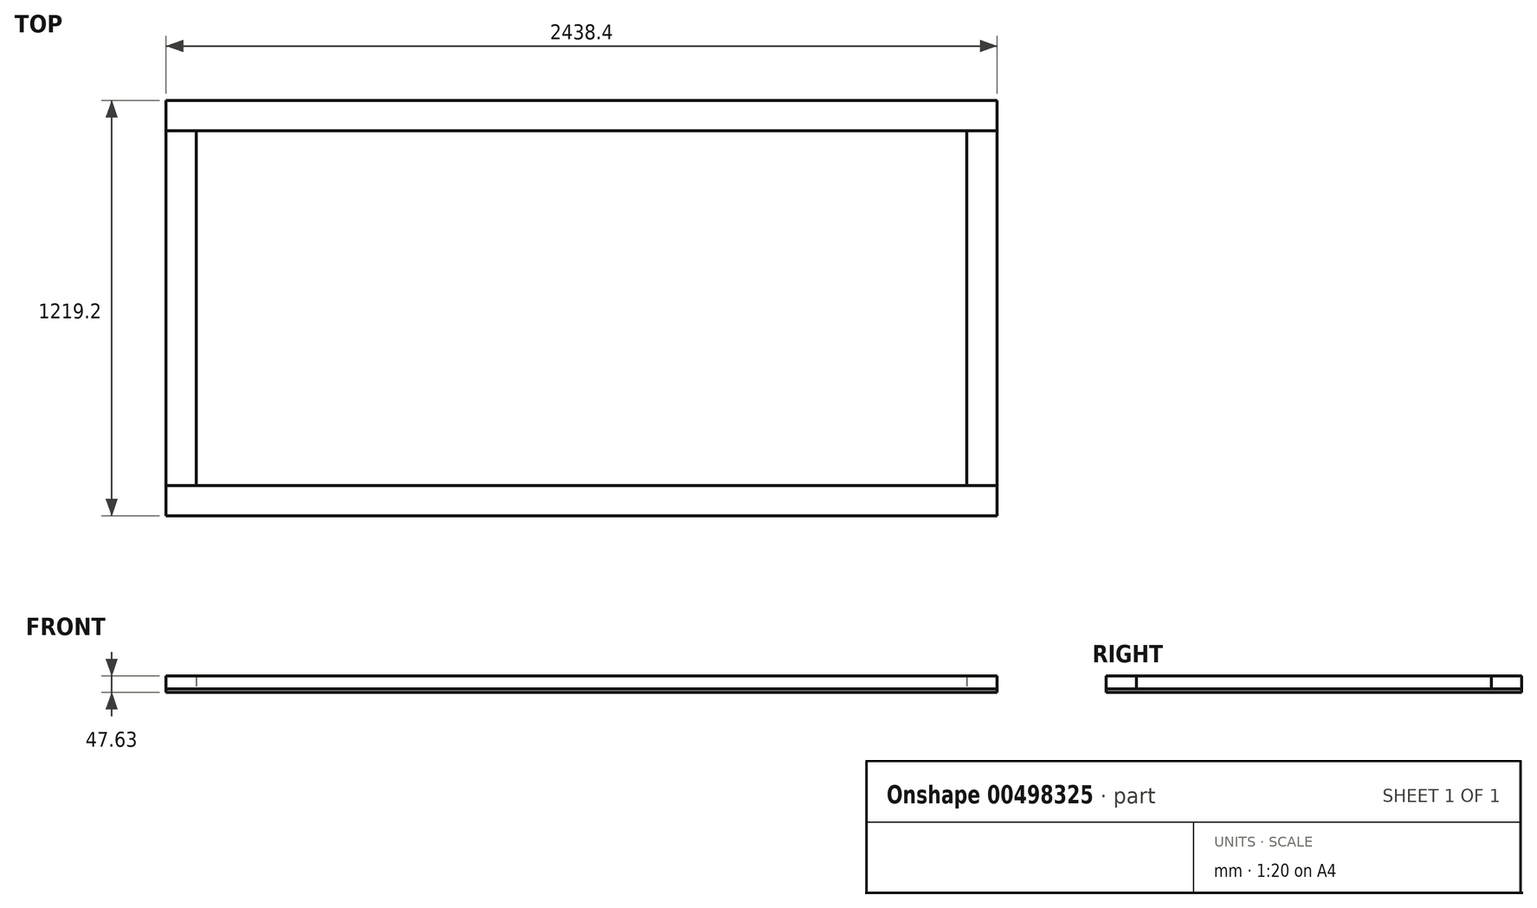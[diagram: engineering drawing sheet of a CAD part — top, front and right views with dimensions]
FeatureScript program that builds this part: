
annotation { "Feature Type Name" : "Feature", "Feature Type Description" : "" }
export const myFeature = defineFeature(function(context is Context, id is Id, definition is map)
    precondition{}
    {
        {
            var Q0;
            Q0=qCreatedBy(makeId("Top.planeOp"),FACE);
            var sketch = newSketch(context, id + "F0", { "sketchPlane" : qUnion([Q0])});
            skLineSegment(sketch, "E0.bottom", {"start": v(1219.2, 609.6) * mm, "end": v(-1219.2, 609.6) * mm});
            skLineSegment(sketch, "E0.top", {"start": v(1219.2, -609.6) * mm, "end": v(-1219.2, -609.6) * mm});
            skLineSegment(sketch, "E0.left", {"start": v(1219.2, 609.6) * mm, "end": v(1219.2, -609.6) * mm});
            skLineSegment(sketch, "E0.right", {"start": v(-1219.2, 609.6) * mm, "end": v(-1219.2, -609.6) * mm});
            skPoint(sketch, "E0.middle", {"position": v(0, 0) * mm});
            skLineSegment(sketch, "E1.bottom", {"start": v(-1130.3, 520.7) * mm, "end": v(1130.3, 520.7) * mm});
            skLineSegment(sketch, "E1.top", {"start": v(-1130.3, -520.7) * mm, "end": v(1130.3, -520.7) * mm});
            skLineSegment(sketch, "E1.left", {"start": v(-1130.3, 520.7) * mm, "end": v(-1130.3, -520.7) * mm});
            skLineSegment(sketch, "E1.right", {"start": v(1130.3, 520.7) * mm, "end": v(1130.3, -520.7) * mm});
            skLineSegment(sketch, "E2", {"start": v(-1130.3, -520.7) * mm, "end": v(-1219.2, -520.7) * mm});
            skLineSegment(sketch, "E3", {"start": v(-1130.3, 520.7) * mm, "end": v(-1219.2, 520.7) * mm});
            skLineSegment(sketch, "E4", {"start": v(1130.3, 520.7) * mm, "end": v(1219.2, 520.7) * mm});
            skLineSegment(sketch, "E5", {"start": v(1130.3, -520.7) * mm, "end": v(1219.2, -520.7) * mm});
            skSolve(sketch);
        }
        {
            var Q0;
            {var subQ1=sQuery(id+"F0.wireOp",EDGE,"E0.bottom");Q0=makeQuery(id+"F0.imprint","IMPRINT",FACE,{"disambiguationData":[TD([[makeQuery(id+"F0.imprint","IMPRINT",EDGE,{"derivedFrom":subQ1}),1.0]])]});}
            var Q1;
            {var subQ1=sQuery(id+"F0.wireOp",EDGE,"E0.top");Q1=makeQuery(id+"F0.imprint","IMPRINT",FACE,{"disambiguationData":[TD([[makeQuery(id+"F0.imprint","IMPRINT",EDGE,{"derivedFrom":subQ1}),-1.0]])]});}
            extrude(context, id + "F1", {"entities" : qUnion([Q0, Q1]), "depth" : 38.1 * mm});
        }
        {
            var Q0;
            Q0=makeQuery(id+"F0.imprint","IMPRINT",FACE,{"disambiguationData":[TD([[makeQuery(id+"F0.imprint","IMPRINT",EDGE,{"derivedFrom":sQuery(id+"F0.wireOp",EDGE,"E1.left")}),-1.0]])]});
            var Q1;
            Q1=makeQuery(id+"F0.imprint","IMPRINT",FACE,{"disambiguationData":[TD([[makeQuery(id+"F0.imprint","IMPRINT",EDGE,{"derivedFrom":sQuery(id+"F0.wireOp",EDGE,"E1.right")}),1.0]])]});
            extrude(context, id + "F2", {"entities" : qUnion([Q0, Q1]), "depth" : 38.1 * mm});
        }
        {
            var Q0;
            {var subQ1=sQuery(id+"F0.wireOp",EDGE,"E0.bottom");Q0=makeQuery(id+"F0.imprint","IMPRINT",FACE,{"disambiguationData":[TD([[makeQuery(id+"F0.imprint","IMPRINT",EDGE,{"derivedFrom":subQ1}),1.0]])]});}
            var Q1;
            Q1=makeQuery(id+"F0.imprint","IMPRINT",FACE,{"disambiguationData":[TD([[makeQuery(id+"F0.imprint","IMPRINT",EDGE,{"derivedFrom":sQuery(id+"F0.wireOp",EDGE,"E1.bottom")}),-1.0]])]});
            var Q2;
            Q2=makeQuery(id+"F0.imprint","IMPRINT",FACE,{"disambiguationData":[TD([[makeQuery(id+"F0.imprint","IMPRINT",EDGE,{"derivedFrom":sQuery(id+"F0.wireOp",EDGE,"E1.left")}),-1.0]])]});
            var Q3;
            {var subQ1=sQuery(id+"F0.wireOp",EDGE,"E0.top");Q3=makeQuery(id+"F0.imprint","IMPRINT",FACE,{"disambiguationData":[TD([[makeQuery(id+"F0.imprint","IMPRINT",EDGE,{"derivedFrom":subQ1}),-1.0]])]});}
            var Q4;
            Q4=makeQuery(id+"F0.imprint","IMPRINT",FACE,{"disambiguationData":[TD([[makeQuery(id+"F0.imprint","IMPRINT",EDGE,{"derivedFrom":sQuery(id+"F0.wireOp",EDGE,"E1.right")}),1.0]])]});
            extrude(context, id + "F3", {"entities" : qUnion([Q0, Q1, Q2, Q3, Q4]), "oppositeDirection" : true, "depth" : 9.52 * mm});
        }
    });
